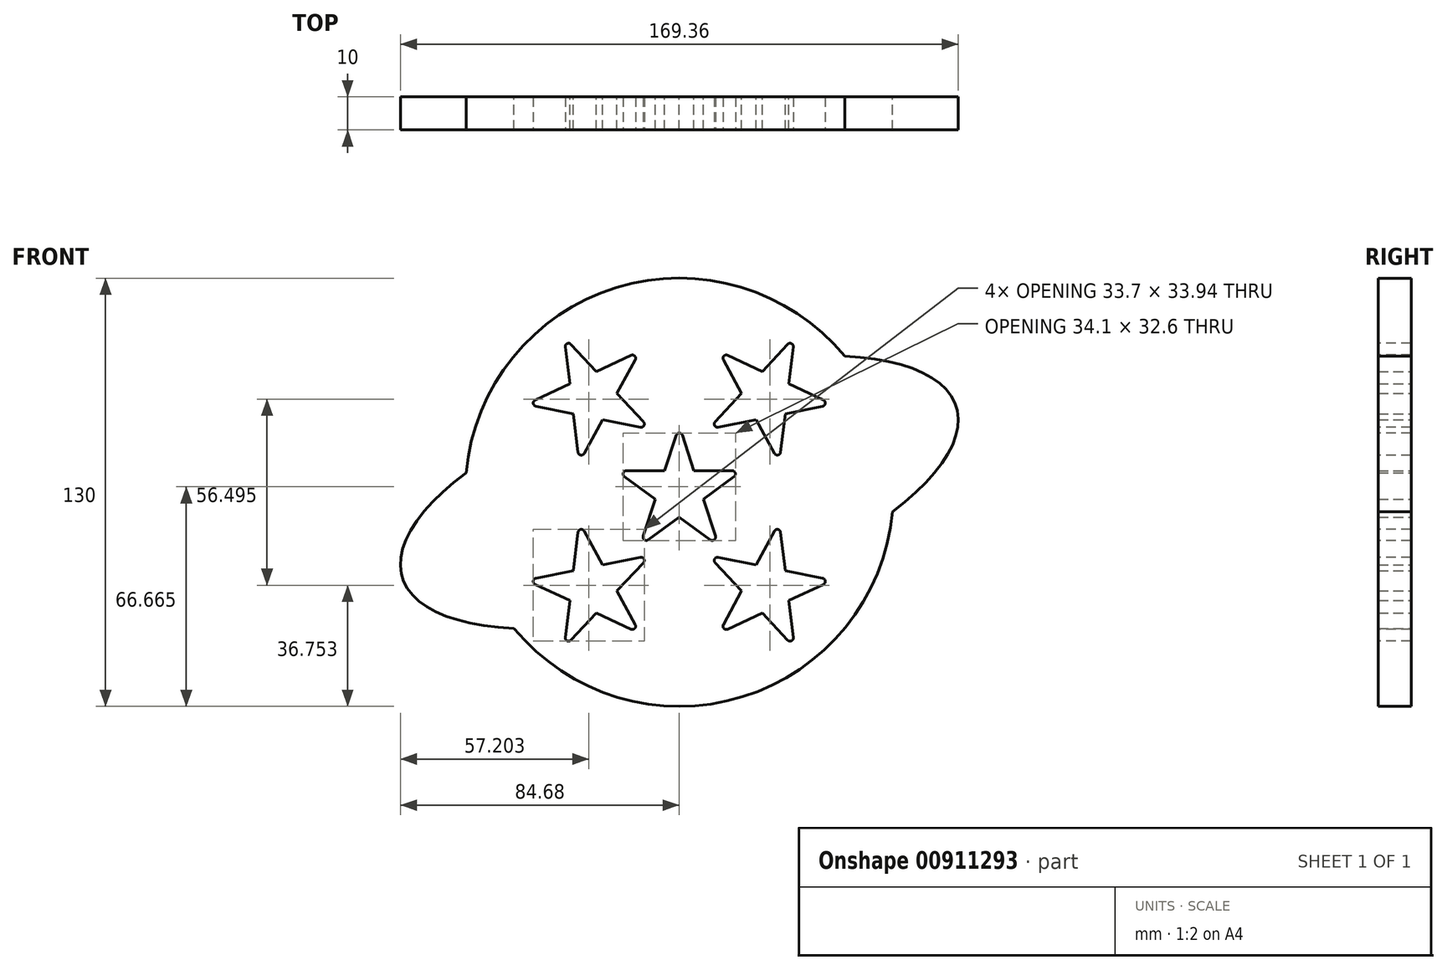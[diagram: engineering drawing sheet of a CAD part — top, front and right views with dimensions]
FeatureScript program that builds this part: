
annotation { "Feature Type Name" : "Feature", "Feature Type Description" : "" }
export const myFeature = defineFeature(function(context is Context, id is Id, definition is map)
    precondition{}
    {
        {
            var Q0;
            Q0=qCreatedBy(makeId("Front.planeOp"),FACE);
            var sketch = newSketch(context, id + "F0", { "sketchPlane" : qUnion([Q0])});
            skArc(sketch, "E0", {"start": v(-50.19, -41.3) * mm, "mid": v(19.14, -62.12) * mm, "end": v(64.73, -5.9) * mm});
            skEllipticalArc(sketch, "E1", {});
            skArc(sketch, "E2.trimOffspring", {"start": v(50.19, 41.3) * mm, "mid": v(-19.14, 62.12) * mm, "end": v(-64.73, 5.9) * mm});
            skEllipticalArc(sketch, "E3.trimOffspring", {});
            skLineSegment(sketch, "E4", {"start": v(-30.36, 9.05) * mm, "end": v(-32.15, 23.82) * mm});
            skLineSegment(sketch, "E5", {"start": v(-34.98, 47.14) * mm, "end": v(-25.17, 36.66) * mm});
            skLineSegment(sketch, "E6", {"start": v(-8.76, 19.12) * mm, "end": v(-23.27, 22.04) * mm});
            skLineSegment(sketch, "E7", {"start": v(-46.52, 26.7) * mm, "end": v(-33.25, 32.9) * mm});
            skLineSegment(sketch, "E8", {"start": v(-11.9, 42.85) * mm, "end": v(-18.93, 30) * mm});
            skLineSegment(sketch, "E9", {"start": v(-34.98, 47.14) * mm, "end": v(-12.27, -1.55) * mm, "construction": true});
            skLineSegment(sketch, "E10", {"start": v(-30.36, 9.05) * mm, "end": v(-8.76, 19.12) * mm, "construction": true});
            skLineSegment(sketch, "E11.MirrorCS", {"start": v(30.36, 9.05) * mm, "end": v(8.76, 19.12) * mm, "construction": true});
            skLineSegment(sketch, "E12.MirrorCS", {"start": v(34.98, 47.14) * mm, "end": v(12.27, -1.55) * mm, "construction": true});
            skLineSegment(sketch, "E13.MirrorCS", {"start": v(34.98, 47.14) * mm, "end": v(25.17, 36.66) * mm});
            skLineSegment(sketch, "E14.MirrorCS", {"start": v(30.36, 9.05) * mm, "end": v(34.98, 47.14) * mm});
            skLineSegment(sketch, "E15.MirrorCS", {"start": v(8.76, 19.12) * mm, "end": v(23.27, 22.04) * mm});
            skLineSegment(sketch, "E16.MirrorCS", {"start": v(11.9, 42.85) * mm, "end": v(18.93, 30) * mm});
            skLineSegment(sketch, "E17.MirrorCS", {"start": v(46.52, 26.7) * mm, "end": v(33.25, 32.9) * mm});
            skLineSegment(sketch, "E18.MirrorCS", {"start": v(-30.36, -9.05) * mm, "end": v(-32.15, -23.82) * mm});
            skLineSegment(sketch, "E19.MirrorCS", {"start": v(34.98, -47.14) * mm, "end": v(12.27, 1.55) * mm, "construction": true});
            skLineSegment(sketch, "E20.MirrorCS", {"start": v(-30.36, -9.05) * mm, "end": v(-8.76, -19.12) * mm, "construction": true});
            skLineSegment(sketch, "E21.MirrorCS", {"start": v(-8.76, -19.12) * mm, "end": v(-23.27, -22.04) * mm});
            skLineSegment(sketch, "E22.MirrorCS", {"start": v(46.52, -26.7) * mm, "end": v(33.25, -32.9) * mm});
            skLineSegment(sketch, "E23.MirrorCS", {"start": v(-11.9, -42.85) * mm, "end": v(-18.93, -30) * mm});
            skLineSegment(sketch, "E24.MirrorCS", {"start": v(34.98, -47.14) * mm, "end": v(25.17, -36.66) * mm});
            skLineSegment(sketch, "E25.MirrorCS", {"start": v(-34.98, -47.14) * mm, "end": v(-25.17, -36.66) * mm});
            skLineSegment(sketch, "E26.MirrorCS", {"start": v(30.36, -9.05) * mm, "end": v(32.15, -23.82) * mm});
            skLineSegment(sketch, "E27.MirrorCS", {"start": v(-46.52, -26.7) * mm, "end": v(-33.25, -32.9) * mm});
            skLineSegment(sketch, "E28.MirrorCS", {"start": v(11.9, -42.85) * mm, "end": v(18.93, -30) * mm});
            skLineSegment(sketch, "E29.MirrorCS", {"start": v(8.76, -19.12) * mm, "end": v(23.27, -22.04) * mm});
            skLineSegment(sketch, "E30.MirrorCS", {"start": v(-34.98, -47.14) * mm, "end": v(-12.27, 1.55) * mm, "construction": true});
            skLineSegment(sketch, "E31.MirrorCS", {"start": v(30.36, -9.05) * mm, "end": v(8.76, -19.12) * mm, "construction": true});
            skLineSegment(sketch, "E32", {"start": v(-11.92, -16.3) * mm, "end": v(-7.3, -2.15) * mm});
            skLineSegment(sketch, "E33", {"start": v(0, 20.18) * mm, "end": v(4.46, 6.54) * mm});
            skLineSegment(sketch, "E34", {"start": v(11.92, -16.3) * mm, "end": v(0, -7.52) * mm});
            skLineSegment(sketch, "E35", {"start": v(-19.1, 6.54) * mm, "end": v(-4.46, 6.54) * mm});
            skLineSegment(sketch, "E36", {"start": v(19.1, 6.54) * mm, "end": v(7.3, -2.15) * mm});
            skLineSegment(sketch, "E37", {"start": v(0, 20.18) * mm, "end": v(0, -33.54) * mm, "construction": true});
            skLineSegment(sketch, "E38", {"start": v(-11.92, -16.3) * mm, "end": v(11.92, -16.3) * mm, "construction": true});
            skLineSegment(sketch, "E39.trimOffspring", {"start": v(-33.25, 32.9) * mm, "end": v(-34.98, 47.14) * mm});
            skLineSegment(sketch, "E40.trimOffspring", {"start": v(-25.17, 36.66) * mm, "end": v(-11.9, 42.85) * mm});
            skLineSegment(sketch, "E41.trimOffspring", {"start": v(-32.15, 23.82) * mm, "end": v(-46.52, 26.7) * mm});
            skLineSegment(sketch, "E42.trimOffspring", {"start": v(-23.27, 22.04) * mm, "end": v(-30.36, 9.05) * mm});
            skLineSegment(sketch, "E43.trimOffspring", {"start": v(-18.93, 30) * mm, "end": v(-8.76, 19.12) * mm});
            skLineSegment(sketch, "E44.trimOffspring", {"start": v(18.93, 30) * mm, "end": v(8.76, 19.12) * mm});
            skLineSegment(sketch, "E45.trimOffspring", {"start": v(25.17, 36.66) * mm, "end": v(11.9, 42.85) * mm});
            skLineSegment(sketch, "E46.trimOffspring", {"start": v(23.27, 22.04) * mm, "end": v(30.36, 9.05) * mm});
            skLineSegment(sketch, "E47.trimOffspring", {"start": v(32.15, 23.82) * mm, "end": v(46.52, 26.7) * mm});
            skLineSegment(sketch, "E48.trimOffspring", {"start": v(4.46, 6.54) * mm, "end": v(19.1, 6.54) * mm});
            skLineSegment(sketch, "E49.trimOffspring", {"start": v(-4.46, 6.54) * mm, "end": v(0, 20.18) * mm});
            skLineSegment(sketch, "E50.trimOffspring", {"start": v(-7.3, -2.15) * mm, "end": v(-19.1, 6.54) * mm});
            skLineSegment(sketch, "E51.trimOffspring", {"start": v(0, -7.52) * mm, "end": v(-11.92, -16.3) * mm});
            skLineSegment(sketch, "E52.trimOffspring", {"start": v(7.3, -2.15) * mm, "end": v(11.92, -16.3) * mm});
            skLineSegment(sketch, "E53.trimOffspring", {"start": v(-32.15, -23.82) * mm, "end": v(-46.52, -26.7) * mm});
            skLineSegment(sketch, "E54.trimOffspring", {"start": v(-33.25, -32.9) * mm, "end": v(-34.98, -47.14) * mm});
            skLineSegment(sketch, "E55.trimOffspring", {"start": v(-25.17, -36.66) * mm, "end": v(-11.9, -42.85) * mm});
            skLineSegment(sketch, "E56.trimOffspring", {"start": v(-23.27, -22.04) * mm, "end": v(-30.36, -9.05) * mm});
            skLineSegment(sketch, "E57.trimOffspring", {"start": v(-18.93, -30) * mm, "end": v(-8.76, -19.12) * mm});
            skLineSegment(sketch, "E58.trimOffspring", {"start": v(23.27, -22.04) * mm, "end": v(30.36, -9.05) * mm});
            skLineSegment(sketch, "E59.trimOffspring", {"start": v(18.93, -30) * mm, "end": v(8.76, -19.12) * mm});
            skLineSegment(sketch, "E60.trimOffspring", {"start": v(32.15, -23.82) * mm, "end": v(46.52, -26.7) * mm});
            skLineSegment(sketch, "E61.trimOffspring", {"start": v(33.25, -32.9) * mm, "end": v(34.98, -47.14) * mm});
            skLineSegment(sketch, "E62.trimOffspring", {"start": v(25.17, -36.66) * mm, "end": v(11.9, -42.85) * mm});
            const initialGuessF0  = {"E1": [0, 0, 0.9556564404442222, 0.2944839008120458, 0.08799327035975489, 0.03382507996009858, 5.464653877132174, 0.8185314300474121], "E3.trimOffspring": [0, 0, 0.9556564404442222, 0.2944839008120458, 0.08799327035975489, 0.03382507996009858, 2.323061223542382, 3.9601240836372043]};
            skSetInitialGuess(sketch, initialGuessF0);
            skSolve(sketch);
        }
        {
            var Q0;
            Q0 = qSketchRegion(id + "F0", true);
            extrude(context, id + "F1", {"entities" : qUnion([Q0]), "depth" : 10 * mm, "offsetDistance" : 25 * mm});
        }
        {
            var Q0;
            Q0=makeQuery(id+"F1.opExtrude","SWEPT_EDGE",EDGE,{"disambiguationData":[OSD([sQuery(id+"F0.wireOp",EDGE,"E5"),sQuery(id+"F0.wireOp",EDGE,"E39.trimOffspring")])]});
            var Q1;
            Q1=makeQuery(id+"F1.opExtrude","SWEPT_EDGE",EDGE,{"disambiguationData":[OSD([sQuery(id+"F0.wireOp",EDGE,"E8"),sQuery(id+"F0.wireOp",EDGE,"E40.trimOffspring")])]});
            var Q2;
            Q2=makeQuery(id+"F1.opExtrude","SWEPT_EDGE",EDGE,{"disambiguationData":[OSD([sQuery(id+"F0.wireOp",EDGE,"E7"),sQuery(id+"F0.wireOp",EDGE,"E41.trimOffspring")])]});
            var Q3;
            Q3=makeQuery(id+"F1.opExtrude","SWEPT_EDGE",EDGE,{"disambiguationData":[OSD([sQuery(id+"F0.wireOp",EDGE,"E4"),sQuery(id+"F0.wireOp",EDGE,"E42.trimOffspring")])]});
            var Q4;
            Q4=makeQuery(id+"F1.opExtrude","SWEPT_EDGE",EDGE,{"disambiguationData":[OSD([sQuery(id+"F0.wireOp",EDGE,"E6"),sQuery(id+"F0.wireOp",EDGE,"E43.trimOffspring")])]});
            var Q5;
            Q5=makeQuery(id+"F1.opExtrude","SWEPT_EDGE",EDGE,{"disambiguationData":[OSD([sQuery(id+"F0.wireOp",EDGE,"E17.MirrorCS"),sQuery(id+"F0.wireOp",EDGE,"E47.trimOffspring")])]});
            var Q6;
            Q6=makeQuery(id+"F1.opExtrude","SWEPT_EDGE",EDGE,{"disambiguationData":[OSD([sQuery(id+"F0.wireOp",EDGE,"E14.MirrorCS"),sQuery(id+"F0.wireOp",EDGE,"E46.trimOffspring")])]});
            var Q7;
            Q7=makeQuery(id+"F1.opExtrude","SWEPT_EDGE",EDGE,{"disambiguationData":[OSD([sQuery(id+"F0.wireOp",EDGE,"E15.MirrorCS"),sQuery(id+"F0.wireOp",EDGE,"E44.trimOffspring")])]});
            var Q8;
            Q8=makeQuery(id+"F1.opExtrude","SWEPT_EDGE",EDGE,{"disambiguationData":[OSD([sQuery(id+"F0.wireOp",EDGE,"E16.MirrorCS"),sQuery(id+"F0.wireOp",EDGE,"E45.trimOffspring")])]});
            var Q9;
            Q9=makeQuery(id+"F1.opExtrude","SWEPT_EDGE",EDGE,{"disambiguationData":[OSD([sQuery(id+"F0.wireOp",EDGE,"E13.MirrorCS"),sQuery(id+"F0.wireOp",EDGE,"E14.MirrorCS")])]});
            var Q10;
            Q10=makeQuery(id+"F1.opExtrude","SWEPT_EDGE",EDGE,{"disambiguationData":[OSD([sQuery(id+"F0.wireOp",EDGE,"E33"),sQuery(id+"F0.wireOp",EDGE,"E49.trimOffspring")])]});
            var Q11;
            Q11=makeQuery(id+"F1.opExtrude","SWEPT_EDGE",EDGE,{"disambiguationData":[OSD([sQuery(id+"F0.wireOp",EDGE,"E36"),sQuery(id+"F0.wireOp",EDGE,"E48.trimOffspring")])]});
            var Q12;
            Q12=makeQuery(id+"F1.opExtrude","SWEPT_EDGE",EDGE,{"disambiguationData":[OSD([sQuery(id+"F0.wireOp",EDGE,"E35"),sQuery(id+"F0.wireOp",EDGE,"E50.trimOffspring")])]});
            var Q13;
            Q13=makeQuery(id+"F1.opExtrude","SWEPT_EDGE",EDGE,{"disambiguationData":[OSD([sQuery(id+"F0.wireOp",EDGE,"E34"),sQuery(id+"F0.wireOp",EDGE,"E52.trimOffspring")])]});
            var Q14;
            Q14=makeQuery(id+"F1.opExtrude","SWEPT_EDGE",EDGE,{"disambiguationData":[OSD([sQuery(id+"F0.wireOp",EDGE,"E32"),sQuery(id+"F0.wireOp",EDGE,"E51.trimOffspring")])]});
            var Q15;
            Q15=makeQuery(id+"F1.opExtrude","SWEPT_EDGE",EDGE,{"disambiguationData":[OSD([sQuery(id+"F0.wireOp",EDGE,"E22.MirrorCS"),sQuery(id+"F0.wireOp",EDGE,"E60.trimOffspring")])]});
            var Q16;
            Q16=makeQuery(id+"F1.opExtrude","SWEPT_EDGE",EDGE,{"disambiguationData":[OSD([sQuery(id+"F0.wireOp",EDGE,"E26.MirrorCS"),sQuery(id+"F0.wireOp",EDGE,"E58.trimOffspring")])]});
            var Q17;
            Q17=makeQuery(id+"F1.opExtrude","SWEPT_EDGE",EDGE,{"disambiguationData":[OSD([sQuery(id+"F0.wireOp",EDGE,"E24.MirrorCS"),sQuery(id+"F0.wireOp",EDGE,"E61.trimOffspring")])]});
            var Q18;
            Q18=makeQuery(id+"F1.opExtrude","SWEPT_EDGE",EDGE,{"disambiguationData":[OSD([sQuery(id+"F0.wireOp",EDGE,"E29.MirrorCS"),sQuery(id+"F0.wireOp",EDGE,"E59.trimOffspring")])]});
            var Q19;
            Q19=makeQuery(id+"F1.opExtrude","SWEPT_EDGE",EDGE,{"disambiguationData":[OSD([sQuery(id+"F0.wireOp",EDGE,"E28.MirrorCS"),sQuery(id+"F0.wireOp",EDGE,"E62.trimOffspring")])]});
            var Q20;
            Q20=makeQuery(id+"F1.opExtrude","SWEPT_EDGE",EDGE,{"disambiguationData":[OSD([sQuery(id+"F0.wireOp",EDGE,"E27.MirrorCS"),sQuery(id+"F0.wireOp",EDGE,"E53.trimOffspring")])]});
            var Q21;
            Q21=makeQuery(id+"F1.opExtrude","SWEPT_EDGE",EDGE,{"disambiguationData":[OSD([sQuery(id+"F0.wireOp",EDGE,"E25.MirrorCS"),sQuery(id+"F0.wireOp",EDGE,"E54.trimOffspring")])]});
            var Q22;
            Q22=makeQuery(id+"F1.opExtrude","SWEPT_EDGE",EDGE,{"disambiguationData":[OSD([sQuery(id+"F0.wireOp",EDGE,"E23.MirrorCS"),sQuery(id+"F0.wireOp",EDGE,"E55.trimOffspring")])]});
            var Q23;
            Q23=makeQuery(id+"F1.opExtrude","SWEPT_EDGE",EDGE,{"disambiguationData":[OSD([sQuery(id+"F0.wireOp",EDGE,"E21.MirrorCS"),sQuery(id+"F0.wireOp",EDGE,"E57.trimOffspring")])]});
            var Q24;
            Q24=makeQuery(id+"F1.opExtrude","SWEPT_EDGE",EDGE,{"disambiguationData":[OSD([sQuery(id+"F0.wireOp",EDGE,"E18.MirrorCS"),sQuery(id+"F0.wireOp",EDGE,"E56.trimOffspring")])]});
            fillet(context, id + "F2", {"entities" : qUnion([Q0, Q1, Q2, Q3, Q4, Q5, Q6, Q7, Q8, Q9, Q10, Q11, Q12, Q13, Q14, Q15, Q16, Q17, Q18, Q19, Q20, Q21, Q22, Q23, Q24]), "radius" : 1 * mm, "tangentPropagation" : true, "allowEdgeOverflow" : false});
        }
    });
